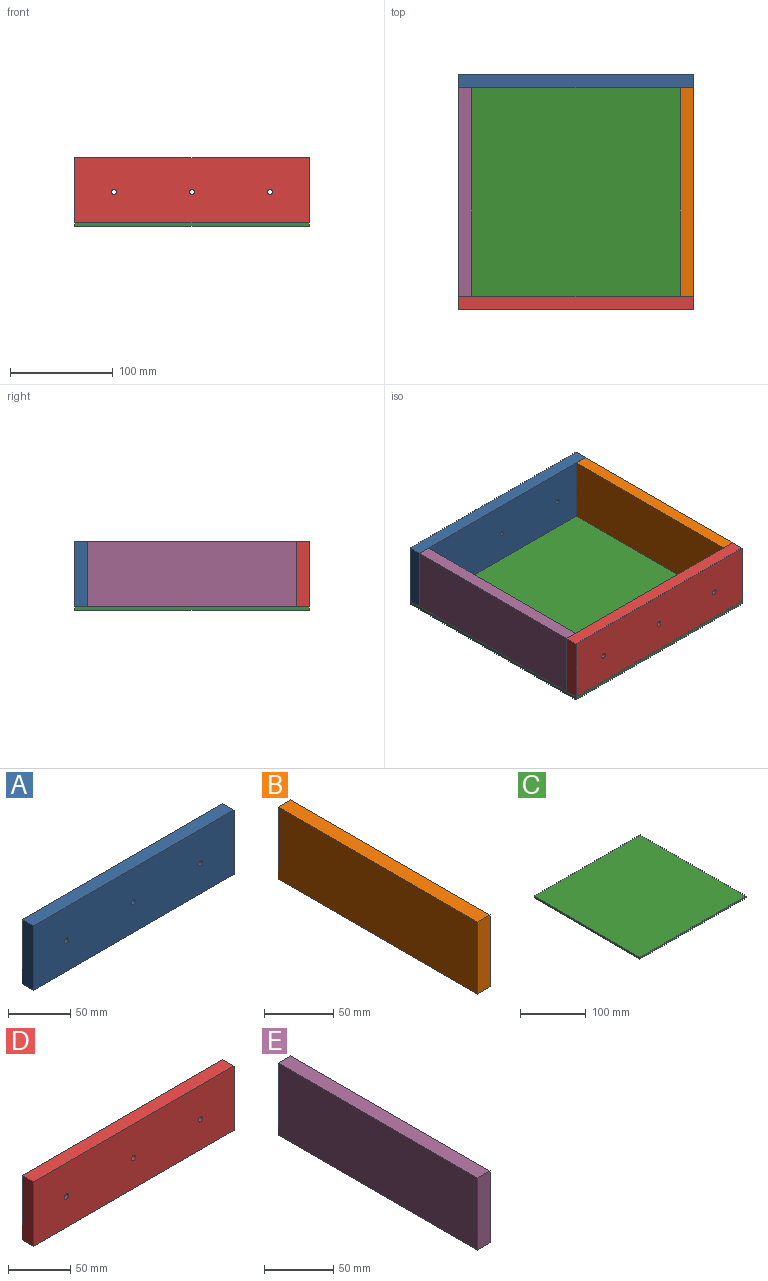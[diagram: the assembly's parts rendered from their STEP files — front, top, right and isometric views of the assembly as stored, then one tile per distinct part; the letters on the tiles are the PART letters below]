
ASSEMBLY  parts=5 mates=4
PART A: 9 faces, bbox 228.6x12.7x63.5 mm
  f0: plane 63.5x12.7mm, normal (-1,0,0), area 806.4mm2, adj f1,f3,f4,f5
  f1: plane 228.6x63.5mm, normal (0,-1,0), area 14457.2mm2, adj f0,f2,f4,f5,f6,f7,f8
  f2: plane 63.5x12.7mm, normal (1,0,0), area 806.5mm2, adj f1,f3,f4,f5
  f3: plane 228.6x63.5mm, normal (0,1,0), area 14457.2mm2, adj f0,f2,f4,f5,f6,f7,f8
  f4: plane 228.6x12.7mm, normal (0,0,1), area 2903.2mm2, adj f0,f1,f2,f3
  f5: plane 228.6x12.7mm, normal (0,0,-1), area 2903.2mm2, adj f0,f1,f2,f3
  f6: cylinder r=2.5mm len=12.7mm, axis (0,-1,0), area 199.5mm2, adj f1,f3
  f7: cylinder r=2.5mm len=12.7mm, axis (0,-1,0), area 199.5mm2, adj f1,f3
  f8: cylinder r=2.5mm len=12.7mm, axis (0,-1,0), area 199.5mm2, adj f1,f3
PART B: 6 faces, bbox 12.7x203.2x63.5 mm
  f0: plane 63.5x12.7mm, normal (0,1,0), area 806.4mm2, adj f1,f3,f4,f5
  f1: plane 203.2x63.5mm, normal (-1,0,0), area 12903.2mm2, adj f0,f2,f4,f5
  f2: plane 63.5x12.7mm, normal (0,-1,0), area 806.5mm2, adj f1,f3,f4,f5
  f3: plane 203.2x63.5mm, normal (1,0,0), area 12903.2mm2, adj f0,f2,f4,f5
  f4: plane 203.2x12.7mm, normal (0,0,1), area 2580.6mm2, adj f0,f1,f2,f3
  f5: plane 203.2x12.7mm, normal (0,0,-1), area 2580.6mm2, adj f0,f1,f2,f3
PART C: 6 faces, bbox 228.6x228.6x3.2 mm
  f0: plane 228.6x3.18mm, normal (-1,0,0), area 725.8mm2, adj f1,f3,f4,f5
  f1: plane 228.6x3.18mm, normal (0,-1,0), area 725.8mm2, adj f0,f2,f4,f5
  f2: plane 228.6x3.18mm, normal (1,0,0), area 725.8mm2, adj f1,f3,f4,f5
  f3: plane 228.6x3.18mm, normal (0,1,0), area 725.8mm2, adj f0,f2,f4,f5
  f4: plane 228.6x228.6mm, normal (0,0,1), area 52258mm2, adj f0,f1,f2,f3
  f5: plane 228.6x228.6mm, normal (0,0,-1), area 52258mm2, adj f0,f1,f2,f3
PART D: 9 faces, bbox 228.6x12.7x63.5 mm
  f0: plane 228.6x63.5mm, normal (0,1,0), area 14457.2mm2, adj f1,f3,f4,f5,f6,f7,f8
  f1: plane 63.5x12.7mm, normal (-1,0,0), area 806.5mm2, adj f0,f2,f4,f5
  f2: plane 228.6x63.5mm, normal (0,-1,0), area 14457.2mm2, adj f1,f3,f4,f5,f6,f7,f8
  f3: plane 63.5x12.7mm, normal (1,0,0), area 806.5mm2, adj f0,f2,f4,f5
  f4: plane 228.6x12.7mm, normal (0,0,1), area 2903.2mm2, adj f0,f1,f2,f3
  f5: plane 228.6x12.7mm, normal (0,0,-1), area 2903.2mm2, adj f0,f1,f2,f3
  f6: cylinder r=2.5mm len=12.7mm, axis (0,-1,0), area 199.5mm2, adj f0,f2
  f7: cylinder r=2.5mm len=12.7mm, axis (0,-1,0), area 199.5mm2, adj f0,f2
  f8: cylinder r=2.5mm len=12.7mm, axis (0,-1,0), area 199.5mm2, adj f0,f2
PART E: 6 faces, bbox 12.7x203.2x63.5 mm
  f0: plane 203.2x63.5mm, normal (1,0,0), area 12903.2mm2, adj f1,f3,f4,f5
  f1: plane 63.5x12.7mm, normal (0,1,0), area 806.4mm2, adj f0,f2,f4,f5
  f2: plane 203.2x63.5mm, normal (-1,0,0), area 12903.2mm2, adj f1,f3,f4,f5
  f3: plane 63.5x12.7mm, normal (0,-1,0), area 806.4mm2, adj f0,f2,f4,f5
  f4: plane 203.2x12.7mm, normal (0,0,1), area 2580.6mm2, adj f0,f1,f2,f3
  f5: plane 203.2x12.7mm, normal (0,0,-1), area 2580.6mm2, adj f0,f1,f2,f3
PLACE A at identity
PLACE B at identity
PLACE C at identity
PLACE D at identity
PLACE E at identity
MATE fastened B.f3 <-> C.f2  axis (1,0,0) through (0,0,107.95)mm
MATE fastened E.f2 <-> C.f0  axis (-1,0,0) through (-228.6,0,107.95)mm
MATE fastened A.f3 <-> C.f3  axis (0,1,0) through (-114.3,114.3,107.95)mm
MATE fastened D.f2 <-> C.f1  axis (0,-1,0) through (-114.3,-114.3,107.95)mm
